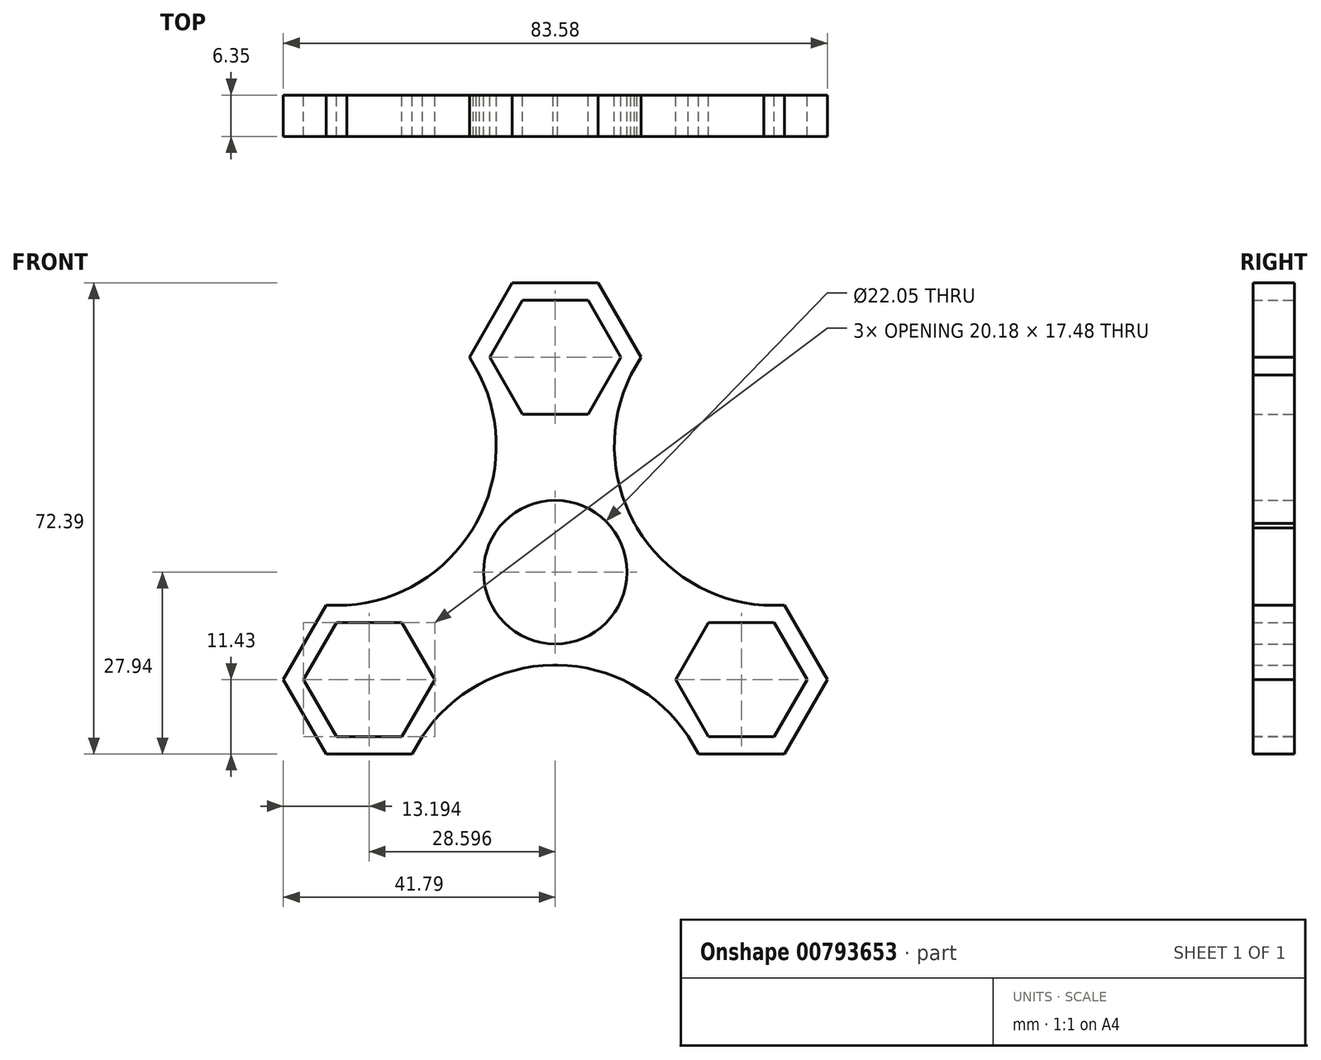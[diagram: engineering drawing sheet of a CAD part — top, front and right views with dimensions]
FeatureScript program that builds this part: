
annotation { "Feature Type Name" : "Feature", "Feature Type Description" : "" }
export const myFeature = defineFeature(function(context is Context, id is Id, definition is map)
    precondition{}
    {
        {
            var Q0;
            Q0=qCreatedBy(makeId("Front.planeOp"),FACE);
            var sketch = newSketch(context, id + "F0", { "sketchPlane" : qUnion([Q0])});
            skCircle(sketch, "E0", {"center": v(0, 0) * mm, "radius": 11.02 * mm});
            skCircle(sketch, "E1", {"center": v(0, 0) * mm, "radius": 14.29 * mm});
            skCircle(sketch, "E2.cCircle", {"center": v(0, 33.02) * mm, "radius": 8.74 * mm, "construction": true});
            skLineSegment(sketch, "E2.0", {"start": v(5.04, 24.28) * mm, "end": v(-5.04, 24.28) * mm});
            skLineSegment(sketch, "E2.1", {"start": v(-5.04, 24.28) * mm, "end": v(-10.09, 33.02) * mm});
            skLineSegment(sketch, "E2.2", {"start": v(-10.09, 33.02) * mm, "end": v(-5.04, 41.76) * mm});
            skLineSegment(sketch, "E2.3", {"start": v(-5.04, 41.76) * mm, "end": v(5.04, 41.76) * mm});
            skLineSegment(sketch, "E2.4", {"start": v(5.04, 41.76) * mm, "end": v(10.09, 33.02) * mm});
            skLineSegment(sketch, "E2.5", {"start": v(10.09, 33.02) * mm, "end": v(5.04, 24.28) * mm});
            skPoint(sketch, "E2.0.midPoint", {"position": v(0, 24.28) * mm});
            skCircle(sketch, "E3.cCircle", {"center": v(0, 33.02) * mm, "radius": 11.43 * mm, "construction": true});
            skLineSegment(sketch, "E3.0", {"start": v(6.6, 21.6) * mm, "end": v(-6.6, 21.6) * mm});
            skLineSegment(sketch, "E3.1", {"start": v(-6.6, 21.59) * mm, "end": v(-13.2, 33.02) * mm});
            skLineSegment(sketch, "E3.2", {"start": v(-13.2, 33.02) * mm, "end": v(-6.6, 44.45) * mm});
            skLineSegment(sketch, "E3.3", {"start": v(-6.6, 44.45) * mm, "end": v(6.6, 44.45) * mm});
            skLineSegment(sketch, "E3.4", {"start": v(6.6, 44.45) * mm, "end": v(13.2, 33.02) * mm});
            skLineSegment(sketch, "E3.5", {"start": v(13.2, 33.02) * mm, "end": v(6.6, 21.6) * mm});
            skPoint(sketch, "E3.0.midPoint", {"position": v(0, 21.6) * mm});
            skLineSegment(sketch, "E4.1.0", {"start": v(-33.64, -25.25) * mm, "end": v(-38.69, -16.5) * mm});
            skLineSegment(sketch, "E4.1.1", {"start": v(-23.55, -25.25) * mm, "end": v(-33.64, -25.25) * mm});
            skCircle(sketch, "E4.1.2", {"center": v(-28.6, -16.5) * mm, "radius": 8.74 * mm, "construction": true});
            skCircle(sketch, "E4.1.3", {"center": v(-28.6, -16.5) * mm, "radius": 11.43 * mm, "construction": true});
            skLineSegment(sketch, "E4.1.4", {"start": v(-35.2, -27.94) * mm, "end": v(-41.8, -16.5) * mm});
            skLineSegment(sketch, "E4.1.5", {"start": v(-22, -27.94) * mm, "end": v(-35.2, -27.94) * mm});
            skLineSegment(sketch, "E4.1.6", {"start": v(-15.4, -16.5) * mm, "end": v(-22, -27.94) * mm});
            skLineSegment(sketch, "E4.1.7", {"start": v(-18.5, -16.5) * mm, "end": v(-23.55, -25.25) * mm});
            skLineSegment(sketch, "E4.1.8", {"start": v(-22, -5.08) * mm, "end": v(-15.4, -16.5) * mm});
            skLineSegment(sketch, "E4.1.9", {"start": v(-23.55, -7.77) * mm, "end": v(-18.5, -16.5) * mm});
            skLineSegment(sketch, "E4.1.10", {"start": v(-41.8, -16.5) * mm, "end": v(-35.2, -5.08) * mm});
            skLineSegment(sketch, "E4.1.11", {"start": v(-35.2, -5.08) * mm, "end": v(-22, -5.08) * mm});
            skLineSegment(sketch, "E4.1.12", {"start": v(-33.64, -7.77) * mm, "end": v(-23.55, -7.77) * mm});
            skLineSegment(sketch, "E4.1.13", {"start": v(-38.69, -16.5) * mm, "end": v(-33.64, -7.77) * mm});
            skLineSegment(sketch, "E4.2.0", {"start": v(38.69, -16.51) * mm, "end": v(33.64, -25.25) * mm});
            skLineSegment(sketch, "E4.2.1", {"start": v(33.64, -7.77) * mm, "end": v(38.69, -16.51) * mm});
            skCircle(sketch, "E4.2.2", {"center": v(28.6, -16.51) * mm, "radius": 8.74 * mm, "construction": true});
            skCircle(sketch, "E4.2.3", {"center": v(28.6, -16.51) * mm, "radius": 11.43 * mm, "construction": true});
            skLineSegment(sketch, "E4.2.4", {"start": v(41.8, -16.51) * mm, "end": v(35.2, -27.94) * mm});
            skLineSegment(sketch, "E4.2.5", {"start": v(35.2, -5.08) * mm, "end": v(41.8, -16.51) * mm});
            skLineSegment(sketch, "E4.2.6", {"start": v(22, -5.08) * mm, "end": v(35.2, -5.08) * mm});
            skLineSegment(sketch, "E4.2.7", {"start": v(23.55, -7.77) * mm, "end": v(33.64, -7.77) * mm});
            skLineSegment(sketch, "E4.2.8", {"start": v(15.4, -16.51) * mm, "end": v(22, -5.08) * mm});
            skLineSegment(sketch, "E4.2.9", {"start": v(18.5, -16.51) * mm, "end": v(23.55, -7.77) * mm});
            skLineSegment(sketch, "E4.2.10", {"start": v(35.2, -27.94) * mm, "end": v(22, -27.94) * mm});
            skLineSegment(sketch, "E4.2.11", {"start": v(22, -27.94) * mm, "end": v(15.4, -16.51) * mm});
            skLineSegment(sketch, "E4.2.12", {"start": v(23.55, -25.25) * mm, "end": v(18.5, -16.51) * mm});
            skLineSegment(sketch, "E4.2.13", {"start": v(33.64, -25.25) * mm, "end": v(23.55, -25.25) * mm});
            skArc(sketch, "E5", {"start": v(-35.2, -5.08) * mm, "mid": v(-12.36, 7.14) * mm, "end": v(-13.2, 33.02) * mm});
            skArc(sketch, "E6", {"start": v(22, -27.94) * mm, "mid": v(0, -14.28) * mm, "end": v(-22, -27.94) * mm});
            skArc(sketch, "E7", {"start": v(13.2, 33.02) * mm, "mid": v(12.37, 7.14) * mm, "end": v(35.2, -5.08) * mm});
            skSolve(sketch);
        }
        {
            var Q0;
            Q0 = qSketchRegion(id + "F0", true);
            extrude(context, id + "F1", {"entities" : qUnion([Q0]), "depth" : 6.35 * mm, "offsetDistance" : 25.4 * mm});
        }
    });
